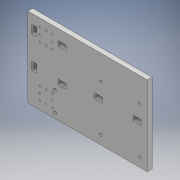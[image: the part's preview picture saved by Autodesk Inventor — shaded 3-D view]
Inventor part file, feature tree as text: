
AUTODESK INVENTOR PART (.ipt)
format: ipt  version: 2017 (Build 210142000, 142)  size: 219,136 bytes
history: native  units: mm
features: sketch x4, extrude x4, other x1, projected_geometry x1
ambient origin geometry x8: Origin, YZ Plane, XZ Plane, XY Plane, X Axis, Y Axis, Z Axis, Center Point
bodies: Body1 (feature_tree)
feature tree (10):
  sketch  "Esquisse1"
  other  "Plan de construction1"
  extrude  "Extrusion2"  Depth=150.0mm
  extrude  "Extrusion3"  Depth=100.0mm
  extrude  "Extrusion4"  Depth=2.1mm
  extrude  "Extrusion5"  Depth=10.0mm
  sketch  "Esquisse3"
  projected_geometry  "Boucle projetée2"
  sketch  "Esquisse4"
  sketch  "Esquisse5"
